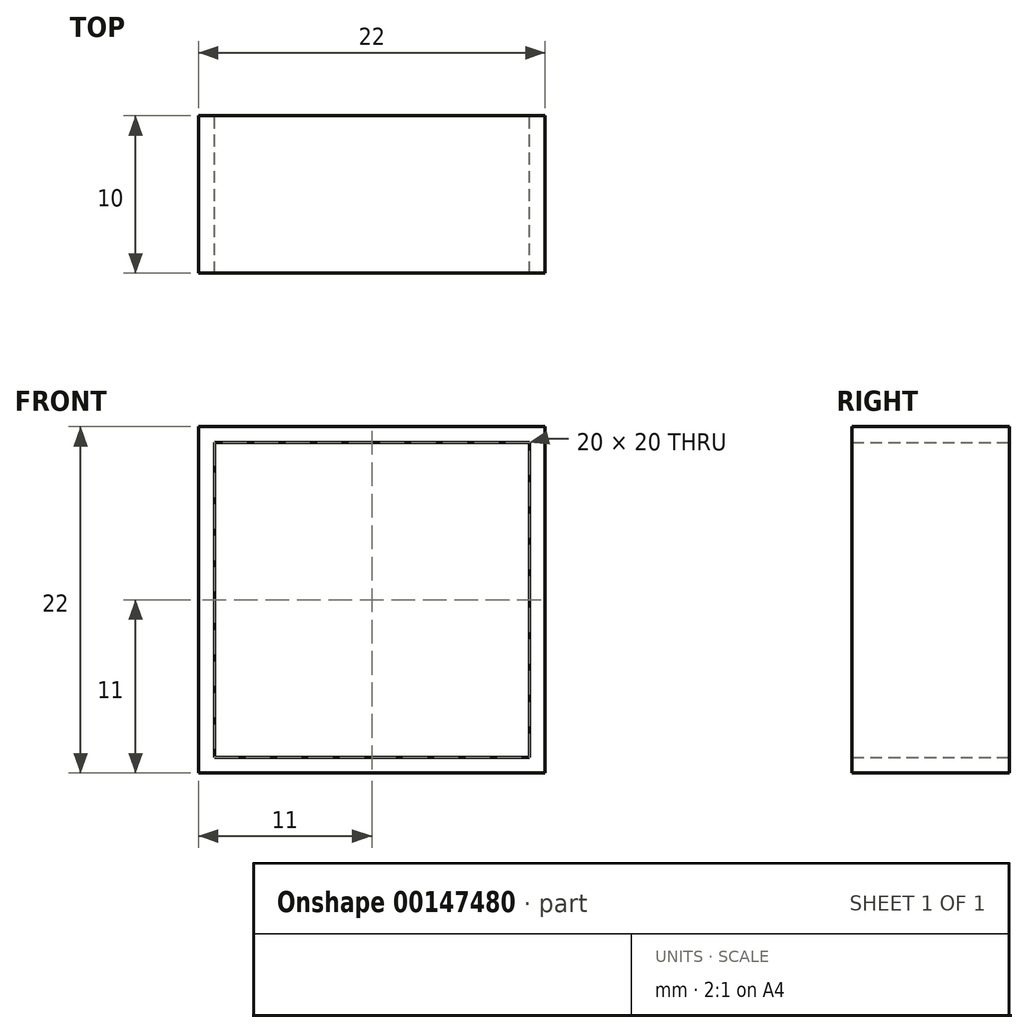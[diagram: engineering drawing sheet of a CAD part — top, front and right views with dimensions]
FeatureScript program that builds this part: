
annotation { "Feature Type Name" : "Feature", "Feature Type Description" : "" }
export const myFeature = defineFeature(function(context is Context, id is Id, definition is map)
    precondition{}
    {
        {
            var Q0;
            Q0=qCreatedBy(makeId("Front.planeOp"),FACE);
            var sketch = newSketch(context, id + "F0", { "sketchPlane" : qUnion([Q0])});
            skLineSegment(sketch, "E0.bottom", {"start": v(10, -10) * mm, "end": v(-10, -10) * mm});
            skLineSegment(sketch, "E0.top", {"start": v(10, 10) * mm, "end": v(-10, 10) * mm});
            skLineSegment(sketch, "E0.left", {"start": v(10, -10) * mm, "end": v(10, 10) * mm});
            skLineSegment(sketch, "E0.right", {"start": v(-10, -10) * mm, "end": v(-10, 10) * mm});
            skPoint(sketch, "E0.middle", {"position": v(0, 0) * mm});
            skLineSegment(sketch, "E1.bottom", {"start": v(11, -11) * mm, "end": v(-11, -11) * mm});
            skLineSegment(sketch, "E1.top", {"start": v(11, 11) * mm, "end": v(-11, 11) * mm});
            skLineSegment(sketch, "E1.left", {"start": v(11, -11) * mm, "end": v(11, 11) * mm});
            skLineSegment(sketch, "E1.right", {"start": v(-11, -11) * mm, "end": v(-11, 11) * mm});
            skSolve(sketch);
        }
        {
            var Q0;
            Q0=makeQuery(id+"F0.imprint","IMPRINT",FACE,{"disambiguationData":[TD([[makeQuery(id+"F0.imprint","IMPRINT",EDGE,{"derivedFrom":sQuery(id+"F0.wireOp",EDGE,"E0.bottom")}),1.0]])]});
            extrude(context, id + "F1", {"entities" : qUnion([Q0]), "depth" : 10 * mm});
        }
    });
